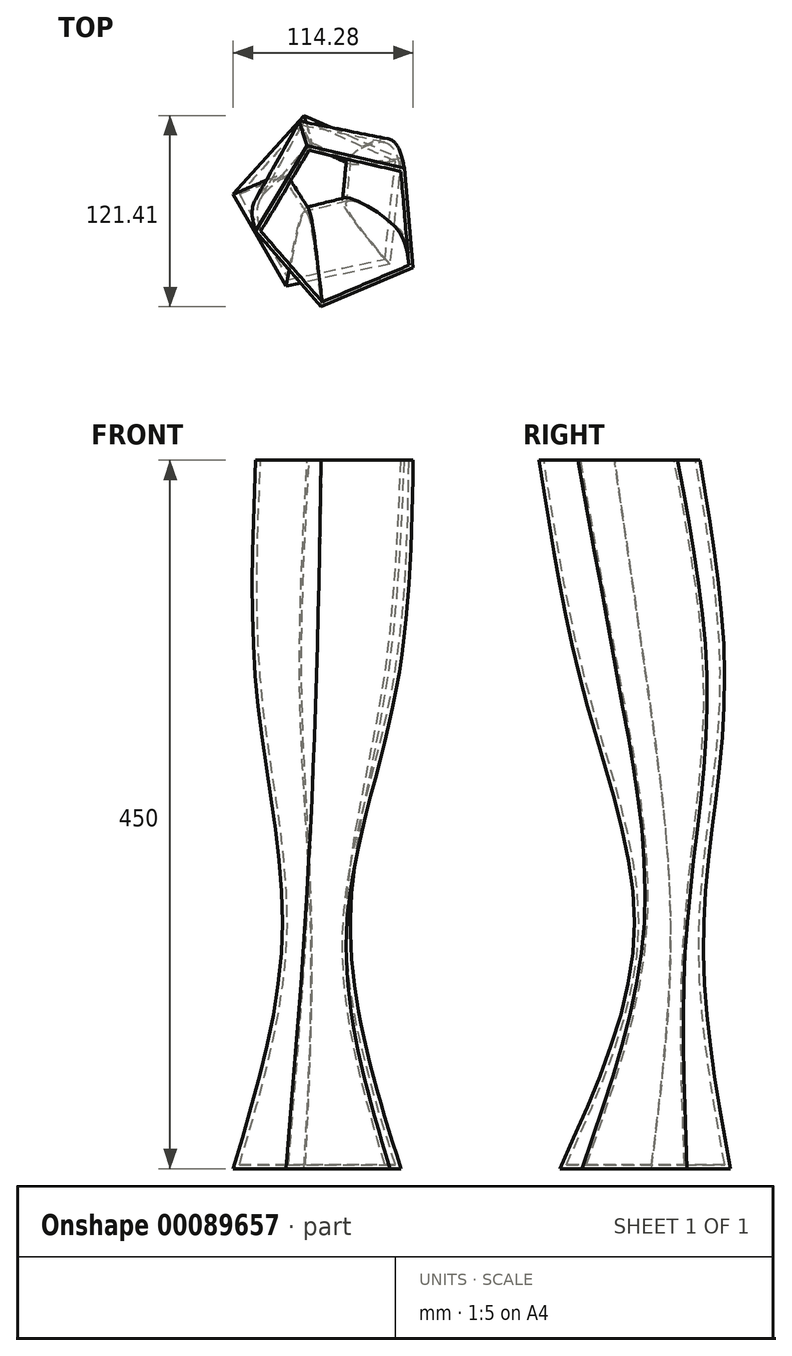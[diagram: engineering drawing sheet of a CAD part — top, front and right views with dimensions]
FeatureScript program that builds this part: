
annotation { "Feature Type Name" : "Feature", "Feature Type Description" : "" }
export const myFeature = defineFeature(function(context is Context, id is Id, definition is map)
    precondition{}
    {
        {
            var Q0;
            Q0=qCreatedBy(makeId("Top.planeOp"),FACE);
            cPlane(context, id + "F0", {"entities" : qUnion([Q0]), "cplaneType" : CPlaneType.OFFSET, "offset" : 150 * mm, "width" : 150 * mm, "height" : 150 * mm});
        }
        {
            var Q0;
            Q0=qCreatedBy(id+"F0.planeOp",FACE);
            cPlane(context, id + "F1", {"entities" : qUnion([Q0]), "cplaneType" : CPlaneType.OFFSET, "offset" : 150 * mm, "width" : 150 * mm, "height" : 150 * mm});
        }
        {
            var Q0;
            Q0=qCreatedBy(id+"F1.planeOp",FACE);
            cPlane(context, id + "F2", {"entities" : qUnion([Q0]), "cplaneType" : CPlaneType.OFFSET, "offset" : 150 * mm, "width" : 150 * mm, "height" : 150 * mm});
        }
        {
            var Q0;
            Q0=qCreatedBy(makeId("Top.planeOp"),FACE);
            var sketch = newSketch(context, id + "F3", { "sketchPlane" : qUnion([Q0])});
            skCircle(sketch, "E0.cCircle", {"center": v(-4.9, -9.63) * mm, "radius": 46.32 * mm, "construction": true});
            skLineSegment(sketch, "E0.0", {"start": v(-61.83, -3.62) * mm, "end": v(-16.78, 46.38) * mm});
            skLineSegment(sketch, "E0.1", {"start": v(-16.78, 46.38) * mm, "end": v(44.7, 18.98) * mm});
            skLineSegment(sketch, "E0.2", {"start": v(44.7, 18.98) * mm, "end": v(37.64, -47.95) * mm});
            skLineSegment(sketch, "E0.3", {"start": v(37.64, -47.95) * mm, "end": v(-28.2, -61.92) * mm});
            skLineSegment(sketch, "E0.4", {"start": v(-28.2, -61.92) * mm, "end": v(-61.83, -3.62) * mm});
            skPoint(sketch, "E0.0.midPoint", {"position": v(-39.3, 21.38) * mm});
            skSolve(sketch);
        }
        {
            var Q0;
            Q0=qCreatedBy(id+"F0.planeOp",FACE);
            var sketch = newSketch(context, id + "F4", { "sketchPlane" : qUnion([Q0])});
            skCircle(sketch, "E1.cCircle", {"center": v(-7.41, 6.73) * mm, "radius": 18.85 * mm, "construction": true});
            skLineSegment(sketch, "E1.0", {"start": v(-30.6, 8.9) * mm, "end": v(-12.52, 29.47) * mm});
            skLineSegment(sketch, "E1.1", {"start": v(-12.52, 29.47) * mm, "end": v(12.63, 18.6) * mm});
            skLineSegment(sketch, "E1.2", {"start": v(12.63, 18.6) * mm, "end": v(10.07, -8.66) * mm});
            skLineSegment(sketch, "E1.3", {"start": v(10.07, -8.66) * mm, "end": v(-16.65, -14.65) * mm});
            skLineSegment(sketch, "E1.4", {"start": v(-16.65, -14.65) * mm, "end": v(-30.6, 8.9) * mm});
            skPoint(sketch, "E1.0.midPoint", {"position": v(-21.56, 19.19) * mm});
            skSolve(sketch);
        }
        {
            var Q0;
            Q0=qCreatedBy(id+"F1.planeOp",FACE);
            var sketch = newSketch(context, id + "F5", { "sketchPlane" : qUnion([Q0])});
            skCircle(sketch, "E2.cCircle", {"center": v(0, 0) * mm, "radius": 38 * mm, "construction": true});
            skLineSegment(sketch, "E2.0", {"start": v(-46.66, -5.34) * mm, "end": v(-19.5, 42.72) * mm});
            skLineSegment(sketch, "E2.1", {"start": v(-19.5, 42.72) * mm, "end": v(34.6, 31.74) * mm});
            skLineSegment(sketch, "E2.2", {"start": v(34.6, 31.74) * mm, "end": v(40.89, -23.1) * mm});
            skLineSegment(sketch, "E2.3", {"start": v(40.89, -23.1) * mm, "end": v(-9.34, -46.02) * mm});
            skLineSegment(sketch, "E2.4", {"start": v(-9.34, -46.02) * mm, "end": v(-46.66, -5.34) * mm});
            skPoint(sketch, "E2.0.midPoint", {"position": v(-33.08, 18.7) * mm});
            skSolve(sketch);
        }
        {
            var Q0;
            Q0=qCreatedBy(id+"F2.planeOp",FACE);
            var sketch = newSketch(context, id + "F6", { "sketchPlane" : qUnion([Q0])});
            skCircle(sketch, "E3.cCircle", {"center": v(6.23, -22.49) * mm, "radius": 43.63 * mm, "construction": true});
            skLineSegment(sketch, "E3.0", {"start": v(-47.5, -27.16) * mm, "end": v(-14.82, 27.16) * mm});
            skLineSegment(sketch, "E3.1", {"start": v(-14.82, 27.16) * mm, "end": v(46.95, 12.88) * mm});
            skLineSegment(sketch, "E3.2", {"start": v(46.95, 12.88) * mm, "end": v(52.45, -50.28) * mm});
            skLineSegment(sketch, "E3.3", {"start": v(52.45, -50.28) * mm, "end": v(-5.92, -75.03) * mm});
            skLineSegment(sketch, "E3.4", {"start": v(-5.92, -75.03) * mm, "end": v(-47.5, -27.16) * mm});
            skPoint(sketch, "E3.0.midPoint", {"position": v(-31.16, 0) * mm});
            skSolve(sketch);
        }
        {
            var Q0;
            Q0=makeQuery(id+"F3.imprint","IMPRINT",FACE,{"disambiguationData":[TD([[makeQuery(id+"F3.imprint","IMPRINT",EDGE,{"derivedFrom":sQuery(id+"F3.wireOp",EDGE,"E0.0")}),-1.0]])]});
            var Q1;
            Q1=makeQuery(id+"F4.imprint","IMPRINT",FACE,{"disambiguationData":[TD([[makeQuery(id+"F4.imprint","IMPRINT",EDGE,{"derivedFrom":sQuery(id+"F4.wireOp",EDGE,"E1.0")}),-1.0]])]});
            var Q2;
            Q2=makeQuery(id+"F5.imprint","IMPRINT",FACE,{"disambiguationData":[TD([[makeQuery(id+"F5.imprint","IMPRINT",EDGE,{"derivedFrom":sQuery(id+"F5.wireOp",EDGE,"E2.0")}),-1.0]])]});
            var Q3;
            Q3=makeQuery(id+"F6.imprint","IMPRINT",FACE,{"disambiguationData":[TD([[makeQuery(id+"F6.imprint","IMPRINT",EDGE,{"derivedFrom":sQuery(id+"F6.wireOp",EDGE,"E3.0")}),-1.0]])]});
            loft(context, id + "F7", {"sheetProfilesArray" : [{ "sheetProfileEntities" : qUnion([Q0]) }, { "sheetProfileEntities" : qUnion([Q1]) }, { "sheetProfileEntities" : qUnion([Q2]) }, { "sheetProfileEntities" : qUnion([Q3]) }]});
        }
        {
            var Q0;
            Q0=makeQuery(id+"F7.opLoft","CAP_FACE",FACE,{"disambiguationData":[OSD([makeQuery(id+"F6.imprint","IMPRINT",FACE,{"disambiguationData":[TD([[makeQuery(id+"F6.imprint","IMPRINT",EDGE,{"derivedFrom":sQuery(id+"F6.wireOp",EDGE,"E3.0")}),-1.0]])]})])],"isStart":true});
            shell(context, id + "F8", {"entities" : qUnion([Q0]), "thickness" : 2.5 * mm});
        }
    });
